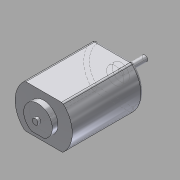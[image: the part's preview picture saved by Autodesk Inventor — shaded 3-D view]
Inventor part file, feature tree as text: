
AUTODESK INVENTOR PART (.ipt)
format: ipt  version: 2015 (Build 190159000, 159)  size: 140,800 bytes
history: native  units: in
note: dims shown in document units (in); Inventor stores cm internally (conversion verified against a paired STEP export)
features: sketch x5, other x3
ambient origin geometry x8: Origin, YZ Plane, XZ Plane, XY Plane, X Axis, Y Axis, Z Axis, Center Point
bodies: Solid1 (feature_tree)
feature tree (8):
  other  "motor_MIR.ipt"
  other  "Solid1::motor_MIR.ipt"
  other  "TaggingFeature1"
  sketch  "Sketch1"  dims[d0=0.3937in]
  sketch  "Sketch2"
  sketch  "Sketch3"
  sketch  "Sketch4"
  sketch  "Sketch5"
